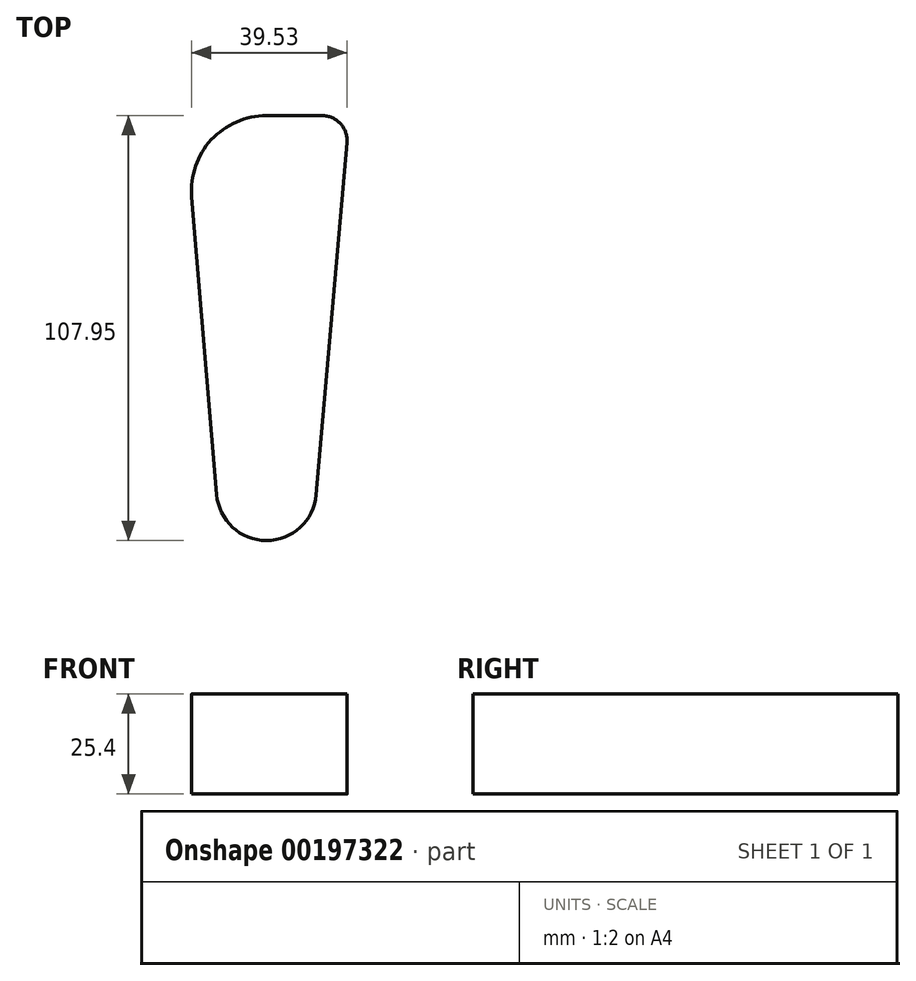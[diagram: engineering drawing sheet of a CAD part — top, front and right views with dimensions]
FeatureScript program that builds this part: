
annotation { "Feature Type Name" : "Feature", "Feature Type Description" : "" }
export const myFeature = defineFeature(function(context is Context, id is Id, definition is map)
    precondition{}
    {
        {
            var Q0;
            Q0=qCreatedBy(makeId("Top.planeOp"),FACE);
            var sketch = newSketch(context, id + "F0", { "sketchPlane" : qUnion([Q0])});
            skCircle(sketch, "E0", {"center": v(-0.27, 0.22) * mm, "radius": 12.7 * mm});
            skArc(sketch, "E1", {"start": v(-0.27, 95.47) * mm, "mid": v(-14.3, 89.32) * mm, "end": v(-19.25, 74.83) * mm});
            skLineSegment(sketch, "E2", {"start": v(-19.25, 74.83) * mm, "end": v(-12.93, -0.84) * mm});
            skLineSegment(sketch, "E3", {"start": v(15.44, 95.47) * mm, "end": v(11.78, 48.97) * mm});
            skArc(sketch, "E4", {"start": v(11.78, 48.97) * mm, "mid": v(12.95, 45.45) * mm, "end": v(16.28, 43.84) * mm});
            skLineSegment(sketch, "E5", {"start": v(-0.27, 95.47) * mm, "end": v(13.86, 95.47) * mm});
            skArc(sketch, "E6.filletArc", {"start": v(20.19, 88.57) * mm, "mid": v(18.54, 93.4) * mm, "end": v(13.86, 95.47) * mm});
            skLineSegment(sketch, "E7", {"start": v(12.38, -0.89) * mm, "end": v(20.19, 88.57) * mm});
            skSolve(sketch);
        }
        {
            var Q0;
            Q0 = qSketchRegion(id + "F0", true);
            extrude(context, id + "F1", {"entities" : qUnion([Q0]), "depth" : 25.4 * mm});
        }
    });
